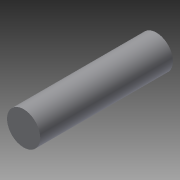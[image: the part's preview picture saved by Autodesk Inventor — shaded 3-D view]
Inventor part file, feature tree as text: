
AUTODESK INVENTOR PART (.ipt)
format: ipt  version: 2014 SP1 (Build 180222100, 222)  size: 70,656 bytes
history: native  units: in
note: dims shown in document units (in); Inventor stores cm internally (conversion verified against a paired STEP export)
features: extrude x1, sketch x1
ambient origin geometry x8: Origin, YZ Plane, XZ Plane, XY Plane, X Axis, Y Axis, Z Axis, Center Point
bodies: Solid1 (feature_tree)
feature tree (2):
  extrude  "Extrusion1"  Depth=1.0in TaperAngle=0.0deg
  sketch  "Sketch1"  dims[d0=0.25in d1=1.0in d2=0.0in]
